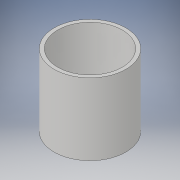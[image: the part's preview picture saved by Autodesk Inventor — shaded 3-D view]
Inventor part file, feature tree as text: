
AUTODESK INVENTOR PART (.ipt)
format: ipt  version: 2019 (Build 230136000, 136)  size: 94,720 bytes
history: native  units: in
note: dims shown in document units (in); Inventor stores cm internally (conversion verified against a paired STEP export)
features: extrude x1, sketch x1
ambient origin geometry x8: Origin, YZ Plane, XZ Plane, XY Plane, X Axis, Y Axis, Z Axis, Center Point
bodies: Solid1 (feature_tree)
feature tree (2):
  extrude  "Extrusion1"  Depth=5.0in
  sketch  "Sketch1"  dims[d0=4.5in d1=0.25in d2=5.0in d3=0.0in]
